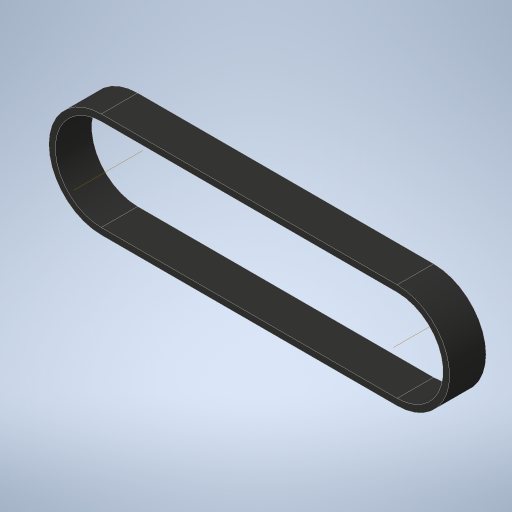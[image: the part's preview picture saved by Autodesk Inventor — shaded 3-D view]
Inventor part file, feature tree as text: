
AUTODESK INVENTOR PART (.ipt)
format: ipt  version: 2023.3 (Build 273359000, 359)  size: 306,688 bytes
history: native  units: in
note: dims shown in document units (in); Inventor stores cm internally (conversion verified against a paired STEP export)
features: sketch x4, extrude x1, other x1, projected_geometry x1
ambient origin geometry x8: Origin, YZ Plane, XZ Plane, XY Plane, X Axis, Y Axis, Z Axis, Center Point
bodies: Body1 (feature_tree)
feature tree (7):
  sketch  "Sketch1"  dims[d0=0.9023in d1=0.9023in]
  sketch  "Sketch2"  dims[d2=1.4174in]
  extrude  "Extrusion2"  Depth=0.9023in
  sketch  "Sketch5"  dims[d5=2.7165in d9=0.0787in d10=0.0598in d11=0.0299in d12=0.0219in d13=0.0219in d14=0.0059in d15=0.0059in d20=0.3346in d21=0.0in d22=0.0787in d23=0.0598in d24=0.0299in d25=0.0219in d26=0.0219in d27=0.0059in d28=0.0059in d29=0.0299in d30=0.0394in d31=0.0787in d32=0.0232in d34=0.0219in d35=0.0in d36=0.0in d37=0.0059in d38=0.0022in d39=0.0022in d40=0.0in d41=0.0in d42=0.0081in d43=0.0081in d44=0.0299in]
  other  "Work Axis1"
  sketch  "Sketch4"  dims[d3=1.4174in]
  projected_geometry  "Projected Loop1"
